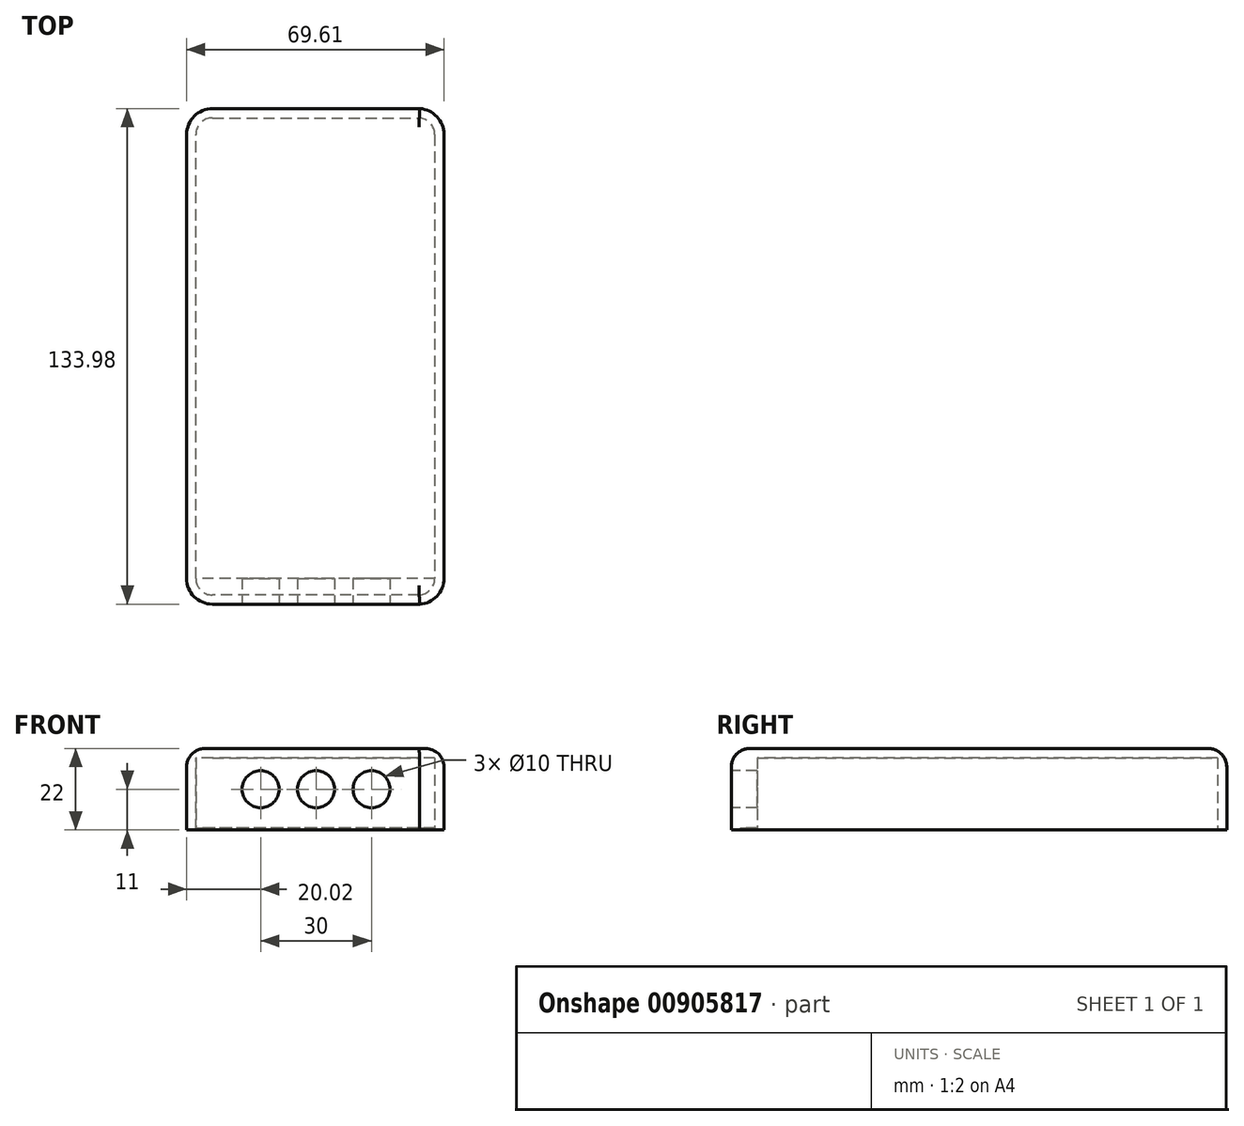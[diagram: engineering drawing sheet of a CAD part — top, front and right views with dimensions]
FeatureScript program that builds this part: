
annotation { "Feature Type Name" : "Feature", "Feature Type Description" : "" }
export const myFeature = defineFeature(function(context is Context, id is Id, definition is map)
    precondition{}
    {
        {
            var Q0;
            Q0=qCreatedBy(makeId("Top.planeOp"),FACE);
            var sketch = newSketch(context, id + "F0", { "sketchPlane" : qUnion([Q0])});
            skLineSegment(sketch, "E0", {"start": v(34.6, 0) * mm, "end": v(34.6, -60) * mm});
            skLineSegment(sketch, "E1", {"start": v(-35.02, -59.99) * mm, "end": v(-35, -0.01) * mm});
            skLineSegment(sketch, "E2", {"start": v(-0.02, -66.99) * mm, "end": v(27.98, -66.99) * mm});
            skLineSegment(sketch, "E3", {"start": v(-0.02, -66.99) * mm, "end": v(-28.02, -66.99) * mm});
            skArc(sketch, "E4", {"start": v(-35.02, -59.99) * mm, "mid": v(-32.97, -64.94) * mm, "end": v(-28.02, -66.99) * mm});
            skArc(sketch, "E5", {"start": v(27.98, -66.99) * mm, "mid": v(32.68, -64.81) * mm, "end": v(34.6, -60) * mm});
            skLineSegment(sketch, "E6", {"start": v(34.6, 0) * mm, "end": v(34.6, 60) * mm});
            skLineSegment(sketch, "E7", {"start": v(-35, -0.01) * mm, "end": v(-35, 59.99) * mm});
            skLineSegment(sketch, "E8", {"start": v(-28, 66.99) * mm, "end": v(28, 66.99) * mm});
            skArc(sketch, "E9", {"start": v(-28, 66.99) * mm, "mid": v(-32.95, 64.94) * mm, "end": v(-35, 59.99) * mm});
            skArc(sketch, "E10", {"start": v(34.6, 60) * mm, "mid": v(32.68, 64.8) * mm, "end": v(28, 66.99) * mm});
            skSolve(sketch);
        }
        {
            var Q0;
            Q0=qSketchRegion(id+"F0",true);
            extrude(context, id + "F1", {"entities" : qUnion([Q0]), "depth" : 11 * mm, "offsetDistance" : 25 * mm});
        }
        {
            var Q0;
            Q0=qSketchRegion(id+"F0",true);
            extrude(context, id + "F2", {"entities" : qUnion([Q0]), "operationType" : NewBodyOperationType.ADD, "depth" : -11 * mm, "offsetDistance" : 25 * mm});
        }
        {
            var Q0;
            Q0=makeQuery(id+"F2.opExtrude","CAP_FACE",FACE,{"disambiguationData":[OSD([sQuery(id+"F0.wireOp",EDGE,"E0"),sQuery(id+"F0.wireOp",EDGE,"E1"),sQuery(id+"F0.wireOp",EDGE,"E2"),sQuery(id+"F0.wireOp",EDGE,"E3"),sQuery(id+"F0.wireOp",EDGE,"E4"),sQuery(id+"F0.wireOp",EDGE,"E5"),sQuery(id+"F0.wireOp",EDGE,"E6"),sQuery(id+"F0.wireOp",EDGE,"E7"),sQuery(id+"F0.wireOp",EDGE,"E8"),sQuery(id+"F0.wireOp",EDGE,"E9"),sQuery(id+"F0.wireOp",EDGE,"E10")])],"isStart":false});
            shell(context, id + "F3", {"entities" : qUnion([Q0]), "thickness" : 2.5 * mm});
        }
        {
            var Q0;
            Q0=makeQuery(id+"F1.opExtrude","CAP_FACE",FACE,{"disambiguationData":[OSD([sQuery(id+"F0.wireOp",EDGE,"E0"),sQuery(id+"F0.wireOp",EDGE,"E1"),sQuery(id+"F0.wireOp",EDGE,"E2"),sQuery(id+"F0.wireOp",EDGE,"E3"),sQuery(id+"F0.wireOp",EDGE,"E4"),sQuery(id+"F0.wireOp",EDGE,"E5"),sQuery(id+"F0.wireOp",EDGE,"E6"),sQuery(id+"F0.wireOp",EDGE,"E7"),sQuery(id+"F0.wireOp",EDGE,"E8"),sQuery(id+"F0.wireOp",EDGE,"E9"),sQuery(id+"F0.wireOp",EDGE,"E10")])],"isStart":false});
            fillet(context, id + "F4", {"entities" : qUnion([Q0]), "radius" : 5 * mm, "tangentPropagation" : true, "allowEdgeOverflow" : false});
        }
        {
            var Q0;
            {var subQ0=sQuery(id+"F0.wireOp",EDGE,"E3");var subQ1=sQuery(id+"F0.wireOp",EDGE,"E2");Q0=makeQuery(id+"F2.boolean.opBoolean","MERGE",FACE,{"derivedFrom":[makeQuery(id+"F1.opExtrude","SWEPT_FACE",FACE,{"disambiguationData":[OSD([subQ1,subQ0])]}),makeQuery(id+"F2.opExtrude","SWEPT_FACE",FACE,{"disambiguationData":[OSD([subQ1,subQ0])]})]});}
            var sketch = newSketch(context, id + "F5", { "sketchPlane" : qUnion([Q0])});
            skCircle(sketch, "E11", {"center": v(15, 0) * mm, "radius": 5 * mm});
            skCircle(sketch, "E12", {"center": v(-15, 0) * mm, "radius": 5 * mm});
            skCircle(sketch, "E13", {"center": v(0, 0) * mm, "radius": 5 * mm});
            skSolve(sketch);
        }
        {
            var Q0;
            Q0=makeQuery(id+"F3.opShell","OFFSET_FACE",FACE,{"disambiguationData":[OSD([sQuery(id+"F0.wireOp",EDGE,"E0"),sQuery(id+"F0.wireOp",EDGE,"E1"),sQuery(id+"F0.wireOp",EDGE,"E2"),sQuery(id+"F0.wireOp",EDGE,"E3"),sQuery(id+"F0.wireOp",EDGE,"E4"),sQuery(id+"F0.wireOp",EDGE,"E5"),sQuery(id+"F0.wireOp",EDGE,"E6"),sQuery(id+"F0.wireOp",EDGE,"E7"),sQuery(id+"F0.wireOp",EDGE,"E8"),sQuery(id+"F0.wireOp",EDGE,"E9"),sQuery(id+"F0.wireOp",EDGE,"E10")])]});
            var sketch = newSketch(context, id + "F6", { "sketchPlane" : qUnion([Q0])});
            skLineSegment(sketch, "E14", {"start": v(0, 64.49) * mm, "end": v(27.9, 64.49) * mm});
            skLineSegment(sketch, "E15", {"start": v(27.9, 64.49) * mm, "end": v(-28.02, 64.49) * mm});
            skLineSegment(sketch, "E16", {"start": v(32.1, 60) * mm, "end": v(-32.52, 59.99) * mm});
            skArc(sketch, "E17", {"start": v(32.1, 60) * mm, "mid": v(30.88, 63.07) * mm, "end": v(27.9, 64.49) * mm});
            skArc(sketch, "E18", {"start": v(-28.02, 64.49) * mm, "mid": v(-31.2, 63.17) * mm, "end": v(-32.52, 59.99) * mm});
            skSolve(sketch);
        }
        {
            var Q0;
            Q0=qSketchRegion(id+"F6",true);
            extrude(context, id + "F7", {"entities" : qUnion([Q0]), "operationType" : NewBodyOperationType.ADD, "depth" : 19 * mm, "offsetDistance" : 25 * mm});
        }
        {
            var Q0;
            Q0=qSketchRegion(id+"F5",true);
            extrude(context, id + "F8", {"entities" : qUnion([Q0]), "operationType" : NewBodyOperationType.REMOVE, "oppositeDirection" : true, "depth" : 8 * mm, "offsetDistance" : 25 * mm});
        }
    });
